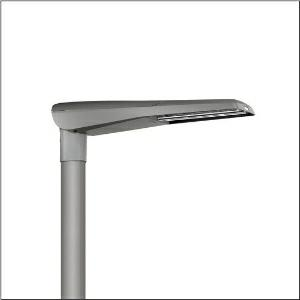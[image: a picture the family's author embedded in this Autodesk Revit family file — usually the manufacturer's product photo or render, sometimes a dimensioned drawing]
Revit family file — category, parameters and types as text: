
# Revit family: streetlight_sl_11_iq_mini___pc-l_5xc2ec1f08he_97a8
name_source: partatom
category: Lighting Fixtures
units: mm (PartAtom-declared; Revit-internal decimal feet)

## family parameters
Cut with Voids When Loaded = No
Host = Face
Light Source = No
Part Type = Normal
Room Calculation Point = No
Round Connector Dimension = Use Diameter
Shared = No

## types (1)
- --- (1 x LED, 5820 lm, 63.6 W, 2200K)
    Apparent Load = 64 VA
    CIE Flux Codes = 37 73 96 100 100
    Color Rendering = 70
    Color Temperature = 2200K
    Default Elevation = 1800 mm
    Description = Streetlight SL 11 iQ mini, mast luminaire, primary light control with 3 zone facetted reflector, of plastic, silver coated, highly specular, primary optical cover: cover, of PMMA, transparent, light distribution: PC-L, light emission: direct distribution, primary light characteristic: asymmetric, left, installation type: post-top, side-entry, lamps: LED, High Power LED, rated values: 7.110lm | 62,2W | 114,3lm/W (begin service life); end service life: 7.110lm | 65,6W; at 50% lumin. flux: 3.555lm | 29,4W | 120,9lm/W, colour temperature: 2200/2700/3000/4000K, colour rendering: CRI > 70, light colour: 722/727/730/740, light setting 1 begin service life: 100% | 7.110lm | 62,2W | 114,3lm/W | 3.000K, light setting 1 end service life: 65,6W, further light settings possible, control: Street-Remote, Auto-Match, Temp-Guard, Lumen-Switch, Night-Set, Smart-Wire, Light-Fading, Desk-Remote (wireless, voltage-free reading and setting of iQ features in the workshop via application-optimized NFC function/RFID function), optimised constant luminous flux control (CLO 2.0), with cable H07RN-F 3x 1.5mm², mains connection: 230..240V, AC, 50/60Hz, connection cable pre-assembled, cable length: 8,5m, luminaire housing, of diecast aluminium, powder-coated, SITECO metallic grey (DB 702S), please order mast flange separately, inclination adjustable without tools: 0°, 5°, 10°, 15° (post-top) | 0°, -5°, -10°, -15° (side-entry), sealing non-destructively replaceable, multi-level sealing system, length: 736mm, width: 174mm, height: 116mm, mast flange for spigot size: 42mm (side-entry): 5XC10008XM4, 60/48mm (side-entry/post-top): 5XC10108XM2, 76/60mm (side-entry/post-top): 5XC10108XM1, equipment: Power, protection rating (complete): IP66, insulation class (complete): insulation class II (safety insulation), certification: CE, ENEC, ENEC+, VDE, impact resistance: IK10, permissible operating ambient temperature for outdoor applications: -25..+50°C, standard-compliant lighting for roads and squares, Environmental Product Declaration (EPD) tested and certified by an independent institute, packaging unit: 1 piece

Light Distribution: PC-L
    Height = 116 mm
    Lamp = 1 x LED
    Lamp Light Flux = 5820 lm
    Lamp Power = 63.6 W
    Lamp count = 1
    Length = 736 mm
    Luminous efficacy = 92 lm/W
    Manufacturer = Siteco
    ModVariant = No
    Model = 5XC2EC1F08HE
    Number of Poles = 1
    OnlyDefault = Yes
    Power Factor = 1
    Product Name = Streetlight SL 11 iQ mini | PC-L
    Product group = mast luminaire | pylon top
    ProductGroupID = 6100
    Protection Class = Protection class II
    Protection Degree = IP 66
    RLX_Detail_Level = 1
    RLX_Emergency_Light_Flux = 0 lm
    RLX_Emergency_Type = 0
    RLX_Emergency_Type_DB = No
    RlxData = <blob elided: 57445 chars, md5=a1dbcceb>
    Socket = socket
    Standby Power = 0 W
    System Light Flux = 5820 lm
    System Power = 64 W
    Type Comments = individual setting: luminous flux: 100 % | dim-lin: 254 | 866 mA
    Type Image = l_1003508.jpg
    URL = http://relux.com
    VarID = @adj_038981
    Voltage = 0 V
    Weight = 0.00 kg
    Width = 174 mm

## geometry (parser evidence)
native form markers: Blend x4, Sweep x12
no freeform markers — native parametric forms only
